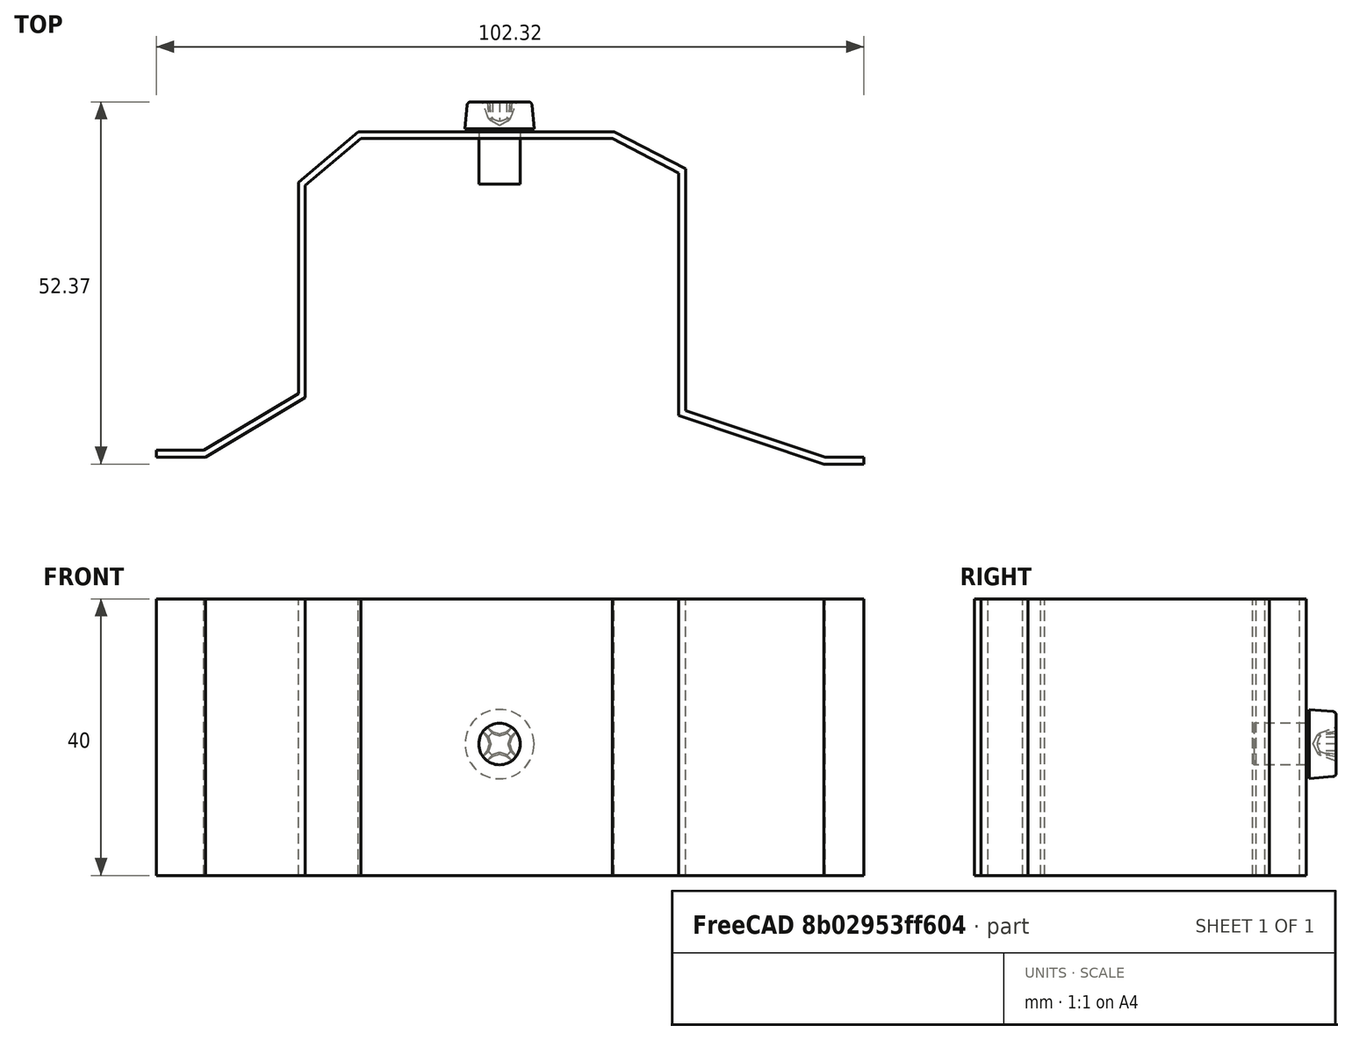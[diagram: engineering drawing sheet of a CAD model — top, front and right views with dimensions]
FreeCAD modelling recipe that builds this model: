
FCSTD DOCUMENT  (FreeCAD 0.21R33771 (Git))
Label: skoba
License: All rights reserved
LicenseURL: http://en.wikipedia.org/wiki/All_rights_reserved
objects: Sketcher::SketchObject×1, PartDesign::Pad×1, PartDesign::Body×1, Part::FeaturePython×1
note: 5 computed .brp shape members not serialized (recipe doc carries the construction recipe); baked Part::Feature solids carry a one-line shape summary decoded from their .brp

FEATURE [Sketcher::SketchObject] Sketch
  FullyConstrained = false
  MapMode = 5
  Support = -> [XY_Plane]
  sketch-geometry (29):
    g0: LineSegment StartX=63.6782 StartY=2.52811 StartZ=0 EndX=57.942 EndY=2.52811 EndZ=0
    g1: LineSegment StartX=57.942 StartY=2.52811 StartZ=0 EndX=36.9068 EndY=9.55842 EndZ=0
    g2: LineSegment StartX=36.9068 StartY=9.55842 StartZ=0 EndX=36.9068 EndY=44.6309 EndZ=0
    g3: LineSegment StartX=36.9068 StartY=44.6309 StartZ=0 EndX=27.33 EndY=49.5954 EndZ=0
    g4: LineSegment StartX=27.33 StartY=49.5954 StartZ=0 EndX=-9.06418 EndY=49.5954 EndZ=0
    g5: LineSegment StartX=-9.06418 StartY=49.5954 StartZ=0 EndX=-17.096 EndY=42.8327 EndZ=0
    g6: LineSegment StartX=-17.096 StartY=42.8327 StartZ=0 EndX=-17.096 EndY=12.1684 EndZ=0
    g7: LineSegment StartX=-17.096 StartY=12.1684 StartZ=0 EndX=-31.5428 EndY=3.54977 EndZ=0
    g8: LineSegment StartX=-31.5428 StartY=3.54977 StartZ=0 EndX=-38.6415 EndY=3.54977 EndZ=0
    g9: LineSegment StartX=-38.6415 StartY=3.54977 StartZ=0 EndX=-38.6415 EndY=4.54977 EndZ=0
    g10: LineSegment StartX=-38.6415 StartY=4.54977 StartZ=0 EndX=-31.8185 EndY=4.54977 EndZ=0
    g11: LineSegment StartX=-31.8185 StartY=4.54977 StartZ=0 EndX=-18.096 EndY=12.7363 EndZ=0
    g12: LineSegment StartX=-18.096 StartY=12.7363 StartZ=0 EndX=-18.096 EndY=43.298 EndZ=0
    g13: LineSegment StartX=-18.096 StartY=43.298 StartZ=0 EndX=-9.42911 EndY=50.5954 EndZ=0
    g14: LineSegment StartX=-9.42911 StartY=50.5954 StartZ=0 EndX=27.5738 EndY=50.5954 EndZ=0
    g15: LineSegment StartX=27.5738 StartY=50.5954 StartZ=0 EndX=37.9068 EndY=45.2389 EndZ=0
    g16: LineSegment StartX=37.9068 StartY=45.2389 StartZ=0 EndX=37.9068 EndY=10.2786 EndZ=0
    g17: LineSegment StartX=37.9068 StartY=10.2786 StartZ=0 EndX=58.1047 EndY=3.52811 EndZ=0
    g18: LineSegment StartX=58.1047 StartY=3.52811 StartZ=0 EndX=63.6782 EndY=3.52811 EndZ=0
    g19: LineSegment StartX=63.6782 StartY=3.52811 StartZ=0 EndX=63.6782 EndY=2.52811 EndZ=0
    g20: GeomPoint X=-17.096 Y=17.8924 Z=0
    g21: GeomPoint X=-21.785 Y=9.37108 Z=0
    g22: GeomPoint X=-35.2089 Y=4.54977 Z=0
    g23: GeomPoint X=-14.0361 Y=46.7164 Z=0
    g24: GeomPoint X=3.97641 Y=50.5954 Z=0
    g25: GeomPoint X=30.506 Y=49.0754 Z=0
    g26: GeomPoint X=37.9068 Y=43.5301 Z=0
    g27: GeomPoint X=36.6104 Y=10.7118 Z=0
    g28: GeomPoint X=39.5222 Y=3.52811 Z=0
  constraints (54):
    c: Coincident(g0,g1)
    c: Coincident(g1,g2)
    c: Vertical(g2)
    c: Coincident(g2,g3)
    c: Coincident(g3,g4)
    c: Coincident(g5,g6)
    c: Vertical(g6)
    c: Coincident(g7,g8)
    c: Horizontal(g8)
    c: Horizontal(g0)
    c: Coincident(g8,g9)
    c: Vertical(g9)
    c: Coincident(g9,g10)
    c: Horizontal(g10)
    c: Coincident(g10,g11)
    c: Coincident(g12,g13)
    c: Horizontal(g14)
    c: Coincident(g14,g15)
    c: Coincident(g15,g16)
    c: Coincident(g16,g17)
    c: Coincident(g17,g18)
    c: Horizontal(g18)
    c: Coincident(g18,g19)
    c: Coincident(g19,g0)
    c: Vertical(g19)
    c: Equal(g19,g9)
    c: DistanceY(g9,g9) = 1
    c: Parallel(g1,g17)
    c: Parallel(g2,g16)
    c: Parallel(g15,g3)
    c: Parallel(g14,g4)
    c: Parallel(g13,g5)
    c: Parallel(g12,g6)
    c: Parallel(g11,g7)
    c: Coincident(g13,g14)
    c: Coincident(g4,g5)
    c: PointOnObject(g20,g6)
    c: Distance(g20,g12) = 1
    c: PointOnObject(g21,g7)
    c: Distance(g21,g11) = 1
    c: PointOnObject(g22,g10)
    c: PointOnObject(g23,g13)
    c: Distance(g23,g5) = 1
    c: PointOnObject(g24,g14)
    c: Distance(g24,g4) = 1
    c: PointOnObject(g25,g15)
    c: Distance(g25,g3) = 1
    c: PointOnObject(g26,g16)
    c: Distance(g26,g2) = 1
    c: PointOnObject(g27,g17)
    c: Distance(g27,g1) = 1
    c: PointOnObject(g28,g18)
    c: Coincident(g11,g12)
    c: Coincident(g6,g7)
FEATURE [PartDesign::Pad] Pad
  Direction = (0,0,1)
  Length = 40
  Length2 = 10
  Profile = -> Sketch
  ReferenceAxis = -> Sketch [N_Axis]
  Refine = true
  Type = 0
FEATURE [PartDesign::Body] Body
  Group = -> [Sketch,Pad]
  Origin = -> Origin
  Tip = -> Pad
FEATURE [Part::FeaturePython] Screw  label="M6x8-Screw"  # Fasteners workbench fastener (typed FeaturePython)
  Placement = pos=(11,51,19) rot=(10,0,0;-1.5708rad)
  diameter = 6
  invert = false
  leftHanded = false
  length = 0
  lengthCustom = 8
  matchOuter = false
  offset = 0
  thread = false
  type = 79
